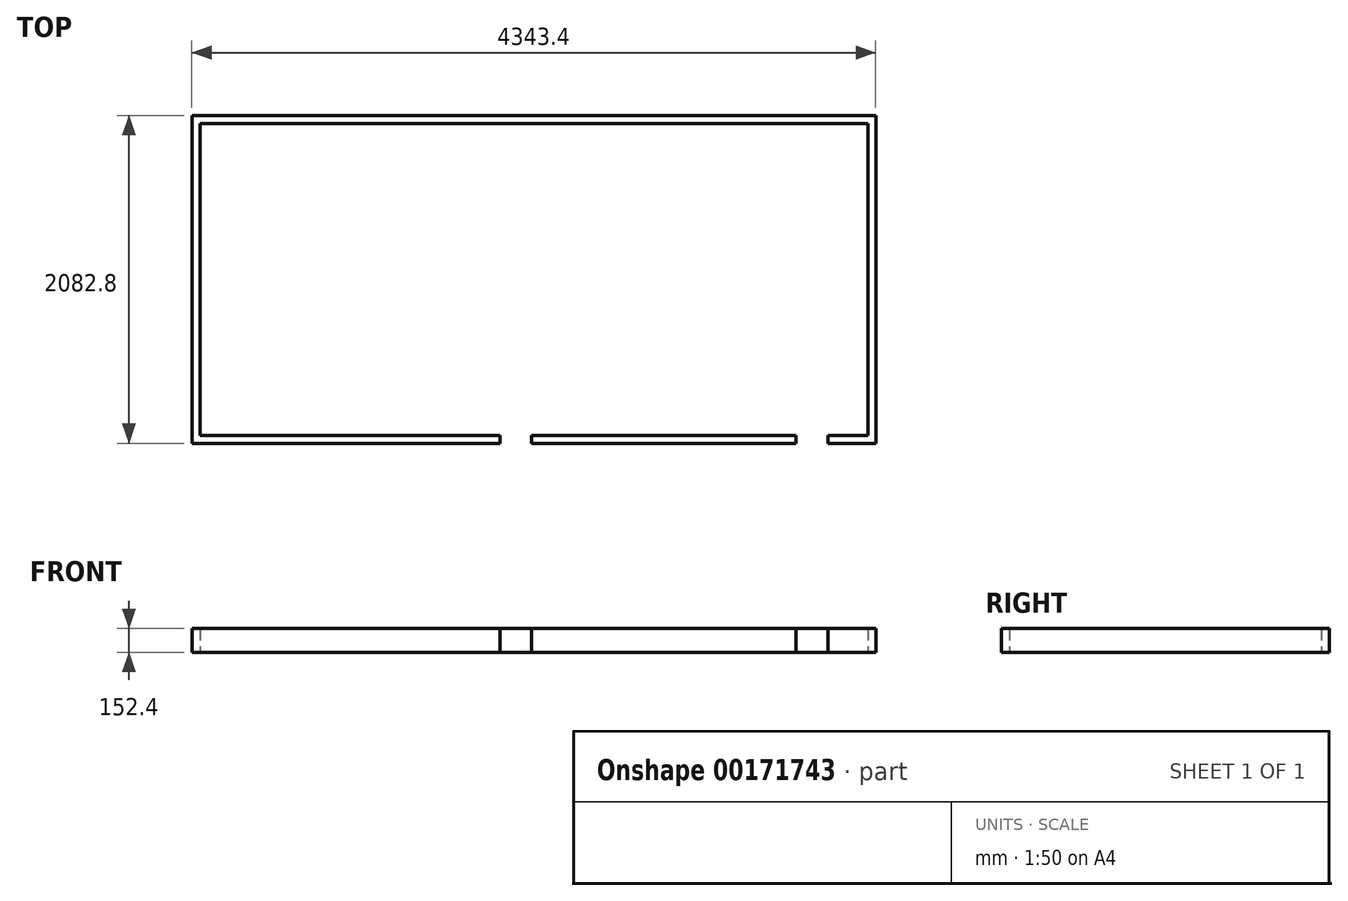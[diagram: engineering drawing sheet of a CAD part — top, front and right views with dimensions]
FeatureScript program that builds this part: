
annotation { "Feature Type Name" : "Feature", "Feature Type Description" : "" }
export const myFeature = defineFeature(function(context is Context, id is Id, definition is map)
    precondition{}
    {
        {
            var Q0;
            Q0=qCreatedBy(makeId("Top.planeOp"),FACE);
            var sketch = newSketch(context, id + "F0", { "sketchPlane" : qUnion([Q0])});
            skLineSegment(sketch, "E0.bottom", {"start": v(-1623.34, 753.12) * mm, "end": v(2618.46, 753.12) * mm});
            skLineSegment(sketch, "E0.top", {"start": v(-1623.34, -1228.08) * mm, "end": v(2618.46, -1228.08) * mm});
            skLineSegment(sketch, "E0.left", {"start": v(-1623.34, 753.12) * mm, "end": v(-1623.34, -1228.08) * mm});
            skLineSegment(sketch, "E0.right", {"start": v(2618.46, 753.12) * mm, "end": v(2618.46, -1228.08) * mm});
            skLineSegment(sketch, "E1.0", {"start": v(-1674.14, -1278.88) * mm, "end": v(2669.26, -1278.88) * mm});
            skLineSegment(sketch, "E1.1", {"start": v(-1674.14, 803.92) * mm, "end": v(-1674.14, -1278.88) * mm});
            skLineSegment(sketch, "E1.2", {"start": v(-1674.14, 803.92) * mm, "end": v(2669.26, 803.92) * mm});
            skLineSegment(sketch, "E1.3", {"start": v(2669.26, 803.92) * mm, "end": v(2669.26, -1278.88) * mm});
            skText(sketch, "E2", { "text": "Wall side", "fontName": "OpenSans-Regular.ttf"});
            const initialGuessF0  = {"E2": [-0.92373, 1.97929, 1, 0, 0.22605]};
            skSetInitialGuess(sketch, initialGuessF0);
            skSolve(sketch);
        }
        {
            var Q0;
            Q0=makeQuery(id+"F0.imprint","IMPRINT",FACE,{"disambiguationData":[TD([[makeQuery(id+"F0.imprint","IMPRINT",EDGE,{"derivedFrom":sQuery(id+"F0.wireOp",EDGE,"E0.bottom")}),1.0]])]});
            extrude(context, id + "F1", {"entities" : qUnion([Q0]), "depth" : 152.4 * mm});
        }
        {
            var Q0;
            Q0=qCreatedBy(makeId("Top.planeOp"),FACE);
            var sketch = newSketch(context, id + "F2", { "sketchPlane" : qUnion([Q0])});
            skLineSegment(sketch, "E3.bottom", {"start": v(281.66, -1215.38) * mm, "end": v(484.86, -1215.38) * mm});
            skLineSegment(sketch, "E3.top", {"start": v(281.66, -1291.58) * mm, "end": v(484.86, -1291.58) * mm});
            skLineSegment(sketch, "E3.left", {"start": v(281.66, -1215.38) * mm, "end": v(281.66, -1291.58) * mm});
            skLineSegment(sketch, "E3.right", {"start": v(484.86, -1215.38) * mm, "end": v(484.86, -1291.58) * mm});
            skLineSegment(sketch, "E4.bottom", {"start": v(2161.26, -1215.38) * mm, "end": v(2364.46, -1215.38) * mm});
            skLineSegment(sketch, "E4.top", {"start": v(2161.26, -1291.58) * mm, "end": v(2364.46, -1291.58) * mm});
            skLineSegment(sketch, "E4.left", {"start": v(2161.26, -1215.38) * mm, "end": v(2161.26, -1291.58) * mm});
            skLineSegment(sketch, "E4.right", {"start": v(2364.46, -1215.38) * mm, "end": v(2364.46, -1291.58) * mm});
            skSolve(sketch);
        }
        {
            var Q0;
            Q0 = qSketchRegion(id + "F2", true);
            extrude(context, id + "F3", {"entities" : qUnion([Q0]), "operationType" : NewBodyOperationType.REMOVE, "endBound" : BoundingType.THROUGH_ALL, "depth" : 25.4 * mm});
        }
    });
